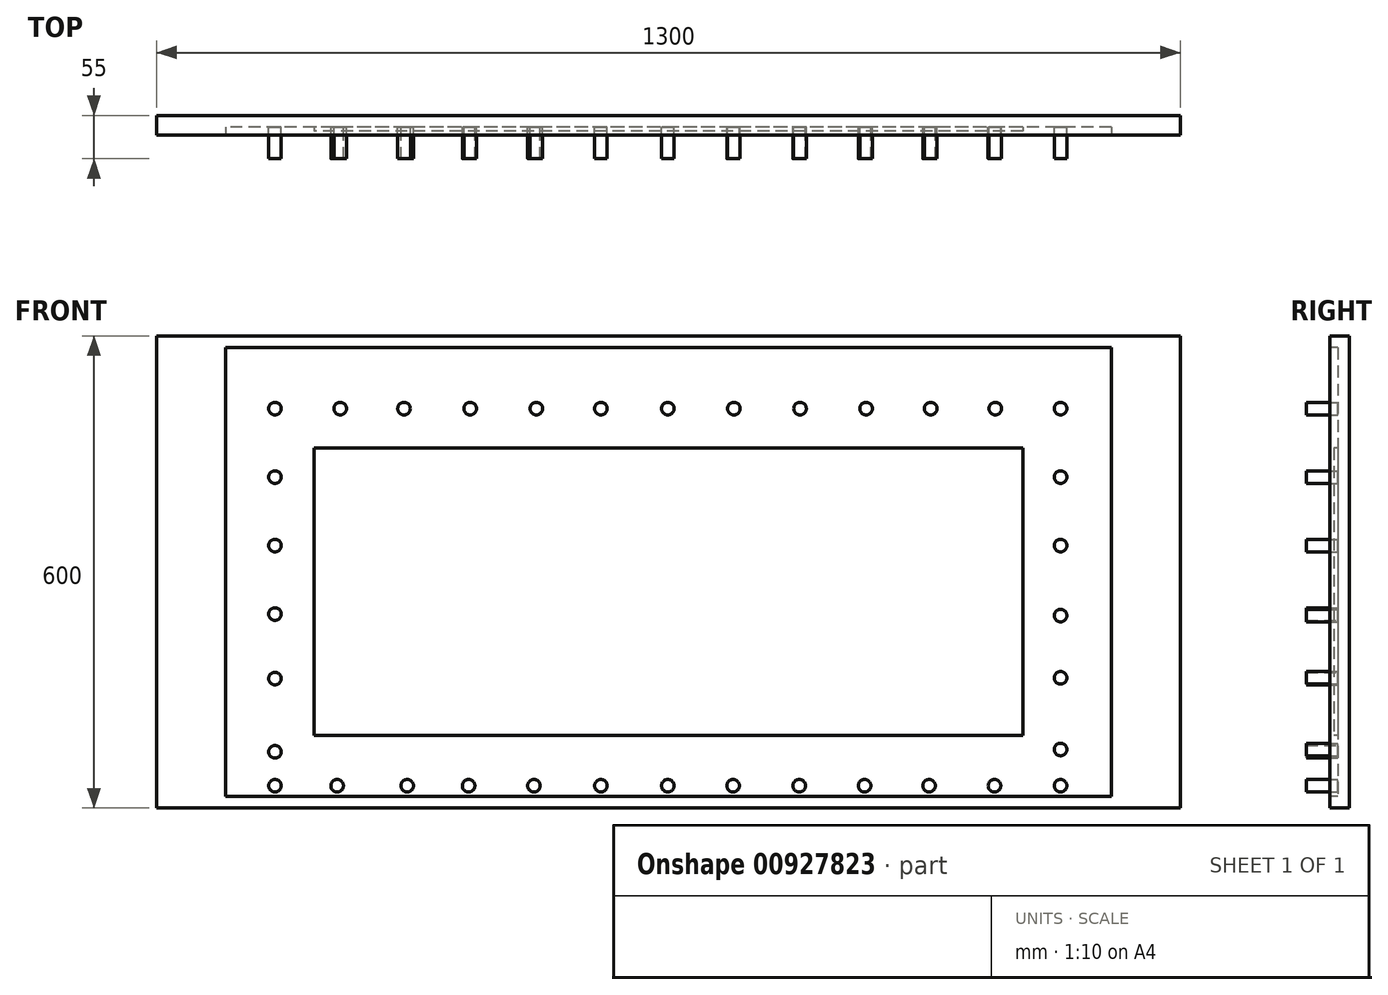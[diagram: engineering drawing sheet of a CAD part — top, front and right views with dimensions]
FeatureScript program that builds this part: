
annotation { "Feature Type Name" : "Feature", "Feature Type Description" : "" }
export const myFeature = defineFeature(function(context is Context, id is Id, definition is map)
    precondition{}
    {
        {
            var Q0;
            Q0=qCreatedBy(makeId("Front.planeOp"),FACE);
            var sketch = newSketch(context, id + "F0", { "sketchPlane" : qUnion([Q0])});
            skLineSegment(sketch, "E0.bottom", {"start": v(-600, 280) * mm, "end": v(600, 280) * mm});
            skLineSegment(sketch, "E0.top", {"start": v(-600, -280) * mm, "end": v(600, -280) * mm});
            skLineSegment(sketch, "E0.left", {"start": v(-600, 280) * mm, "end": v(-600, -280) * mm});
            skLineSegment(sketch, "E0.right", {"start": v(600, 280) * mm, "end": v(600, -280) * mm});
            skPoint(sketch, "E0.middle", {"position": v(0, 0) * mm});
            skCircle(sketch, "E1", {"center": v(550, 237.5) * mm, "radius": 9 * mm});
            skLineSegment(sketch, "E2", {"start": v(550, 237.5) * mm, "end": v(425, 237.5) * mm, "construction": true});
            skLineSegment(sketch, "E3", {"start": v(425, 237.5) * mm, "end": v(340, 237.5) * mm, "construction": true});
            skCircle(sketch, "E4", {"center": v(425, 237.5) * mm, "radius": 9 * mm});
            skCircle(sketch, "E5", {"center": v(340, 237.5) * mm, "radius": 9 * mm});
            skLineSegment(sketch, "E6", {"start": v(340, 237.5) * mm, "end": v(255, 237.5) * mm, "construction": true});
            skLineSegment(sketch, "E7", {"start": v(255, 237.5) * mm, "end": v(170, 237.5) * mm, "construction": true});
            skLineSegment(sketch, "E8", {"start": v(170, 237.5) * mm, "end": v(85, 237.5) * mm, "construction": true});
            skLineSegment(sketch, "E9", {"start": v(85, 237.5) * mm, "end": v(0, 237.5) * mm, "construction": true});
            skLineSegment(sketch, "E10", {"start": v(0, 237.5) * mm, "end": v(-85, 237.5) * mm, "construction": true});
            skLineSegment(sketch, "E11", {"start": v(-85, 237.5) * mm, "end": v(-170, 237.5) * mm, "construction": true});
            skLineSegment(sketch, "E12", {"start": v(-170, 237.5) * mm, "end": v(-255, 237.5) * mm, "construction": true});
            skLineSegment(sketch, "E13", {"start": v(-255, 237.5) * mm, "end": v(-340, 237.5) * mm, "construction": true});
            skLineSegment(sketch, "E14", {"start": v(-340, 237.5) * mm, "end": v(-425, 237.5) * mm, "construction": true});
            skLineSegment(sketch, "E15", {"start": v(-425, 237.5) * mm, "end": v(-550, 237.5) * mm, "construction": true});
            skCircle(sketch, "E16", {"center": v(255, 237.5) * mm, "radius": 9 * mm});
            skCircle(sketch, "E17", {"center": v(170, 237.5) * mm, "radius": 9 * mm});
            skCircle(sketch, "E18", {"center": v(85, 237.5) * mm, "radius": 9 * mm});
            skCircle(sketch, "E19", {"center": v(0, 237.5) * mm, "radius": 9 * mm});
            skCircle(sketch, "E20", {"center": v(-85, 237.5) * mm, "radius": 9 * mm});
            skCircle(sketch, "E21", {"center": v(-170, 237.5) * mm, "radius": 9 * mm});
            skCircle(sketch, "E22", {"center": v(-255, 237.5) * mm, "radius": 9 * mm});
            skCircle(sketch, "E23", {"center": v(-340, 237.5) * mm, "radius": 9 * mm});
            skCircle(sketch, "E24", {"center": v(-425, 237.5) * mm, "radius": 9 * mm});
            skCircle(sketch, "E25", {"center": v(-550, 237.5) * mm, "radius": 9 * mm});
            skLineSegment(sketch, "E26", {"start": v(0, 0) * mm, "end": v(136, 0) * mm, "construction": true});
            skLineSegment(sketch, "E27", {"start": v(0, 0) * mm, "end": v(0, -117.51) * mm, "construction": true});
            skCircle(sketch, "E28.MirrorC", {"center": v(0, -237.5) * mm, "radius": 9 * mm});
            skCircle(sketch, "E29.MirrorC", {"center": v(425, -237.5) * mm, "radius": 9 * mm});
            skCircle(sketch, "E30.MirrorC", {"center": v(340, -237.5) * mm, "radius": 9 * mm});
            skCircle(sketch, "E31.MirrorC", {"center": v(-425, -237.5) * mm, "radius": 9 * mm});
            skCircle(sketch, "E32.MirrorC", {"center": v(85, -237.5) * mm, "radius": 9 * mm});
            skCircle(sketch, "E33.MirrorC", {"center": v(-340, -237.5) * mm, "radius": 9 * mm});
            skCircle(sketch, "E34.MirrorC", {"center": v(-170, -237.5) * mm, "radius": 9 * mm});
            skCircle(sketch, "E35.MirrorC", {"center": v(255, -237.5) * mm, "radius": 9 * mm});
            skCircle(sketch, "E36.MirrorC", {"center": v(-85, -237.5) * mm, "radius": 9 * mm});
            skCircle(sketch, "E37.MirrorC", {"center": v(170, -237.5) * mm, "radius": 9 * mm});
            skCircle(sketch, "E38.MirrorC", {"center": v(-255, -237.5) * mm, "radius": 9 * mm});
            skCircle(sketch, "E39.MirrorC", {"center": v(-550, -237.5) * mm, "radius": 9 * mm});
            skCircle(sketch, "E40.MirrorC", {"center": v(550, -237.5) * mm, "radius": 9 * mm});
            skLineSegment(sketch, "E41.MirrorCS", {"start": v(0, -237.5) * mm, "end": v(-85, -237.5) * mm, "construction": true});
            skLineSegment(sketch, "E42.MirrorCS", {"start": v(340, -237.5) * mm, "end": v(255, -237.5) * mm, "construction": true});
            skLineSegment(sketch, "E43.MirrorCS", {"start": v(170, -237.5) * mm, "end": v(85, -237.5) * mm, "construction": true});
            skLineSegment(sketch, "E44.MirrorCS", {"start": v(-255, -237.5) * mm, "end": v(-340, -237.5) * mm, "construction": true});
            skLineSegment(sketch, "E45.MirrorCS", {"start": v(-85, -237.5) * mm, "end": v(-170, -237.5) * mm, "construction": true});
            skLineSegment(sketch, "E46.MirrorCS", {"start": v(85, -237.5) * mm, "end": v(0, -237.5) * mm, "construction": true});
            skLineSegment(sketch, "E47.MirrorCS", {"start": v(-170, -237.5) * mm, "end": v(-255, -237.5) * mm, "construction": true});
            skLineSegment(sketch, "E48.MirrorCS", {"start": v(425, -237.5) * mm, "end": v(340, -237.5) * mm, "construction": true});
            skLineSegment(sketch, "E49.MirrorCS", {"start": v(550, -237.5) * mm, "end": v(425, -237.5) * mm, "construction": true});
            skLineSegment(sketch, "E50.MirrorCS", {"start": v(-340, -237.5) * mm, "end": v(-425, -237.5) * mm, "construction": true});
            skLineSegment(sketch, "E51.MirrorCS", {"start": v(-425, -237.5) * mm, "end": v(-550, -237.5) * mm, "construction": true});
            skLineSegment(sketch, "E52.MirrorCS", {"start": v(255, -237.5) * mm, "end": v(170, -237.5) * mm, "construction": true});
            skLineSegment(sketch, "E53", {"start": v(550, -237.5) * mm, "end": v(550, -187.5) * mm, "construction": true});
            skLineSegment(sketch, "E54", {"start": v(550, -187.5) * mm, "end": v(550, -102.5) * mm, "construction": true});
            skLineSegment(sketch, "E55", {"start": v(550, -102.5) * mm, "end": v(550, -17.5) * mm, "construction": true});
            skLineSegment(sketch, "E56", {"start": v(550, -17.5) * mm, "end": v(550, 67.5) * mm, "construction": true});
            skLineSegment(sketch, "E57", {"start": v(550, 67.5) * mm, "end": v(550, 152.5) * mm, "construction": true});
            skCircle(sketch, "E58", {"center": v(550, 152.5) * mm, "radius": 9 * mm});
            skCircle(sketch, "E59", {"center": v(550, 67.5) * mm, "radius": 9 * mm});
            skCircle(sketch, "E60", {"center": v(550, -17.5) * mm, "radius": 9 * mm});
            skCircle(sketch, "E61", {"center": v(550, -102.5) * mm, "radius": 9 * mm});
            skCircle(sketch, "E62", {"center": v(550, -187.5) * mm, "radius": 9 * mm});
            skCircle(sketch, "E63.MirrorC", {"center": v(-550, 152.5) * mm, "radius": 9 * mm});
            skLineSegment(sketch, "E64.MirrorCS", {"start": v(-550, -187.5) * mm, "end": v(-550, -102.5) * mm, "construction": true});
            skLineSegment(sketch, "E65.MirrorCS", {"start": v(-550, -17.5) * mm, "end": v(-550, 67.5) * mm, "construction": true});
            skCircle(sketch, "E66.MirrorC", {"center": v(-550, -187.5) * mm, "radius": 9 * mm});
            skCircle(sketch, "E67.MirrorC", {"center": v(-550, -17.5) * mm, "radius": 9 * mm});
            skCircle(sketch, "E68.MirrorC", {"center": v(-550, 67.5) * mm, "radius": 9 * mm});
            skLineSegment(sketch, "E69.MirrorCS", {"start": v(-550, -102.5) * mm, "end": v(-550, -17.5) * mm, "construction": true});
            skLineSegment(sketch, "E70.MirrorCS", {"start": v(-550, 67.5) * mm, "end": v(-550, 152.5) * mm, "construction": true});
            skCircle(sketch, "E71.MirrorC", {"center": v(-550, -102.5) * mm, "radius": 9 * mm});
            skSolve(sketch);
        }
        {
            var Q0;
            Q0 = qSketchRegion(id + "F0", true);
            extrude(context, id + "F1", {"entities" : qUnion([Q0]), "depth" : 20 * mm, "offsetDistance" : 25 * mm});
        }
        {
            var Q0;
            Q0=qCreatedBy(makeId("Front.planeOp"),FACE);
            var sketch = newSketch(context, id + "F2", { "sketchPlane" : qUnion([Q0])});
            skLineSegment(sketch, "E72.bottom", {"start": v(650, 300) * mm, "end": v(-650, 300) * mm});
            skLineSegment(sketch, "E72.top", {"start": v(650, -300) * mm, "end": v(-650, -300) * mm});
            skLineSegment(sketch, "E72.left", {"start": v(650, 300) * mm, "end": v(650, -300) * mm});
            skLineSegment(sketch, "E72.right", {"start": v(-650, 300) * mm, "end": v(-650, -300) * mm});
            skPoint(sketch, "E72.middle", {"position": v(0, 0) * mm});
            skLineSegment(sketch, "E73.bottom", {"start": v(450, 157.5) * mm, "end": v(-450, 157.5) * mm});
            skLineSegment(sketch, "E74", {"start": v(450, 157.5) * mm, "end": v(450, -207.5) * mm});
            skLineSegment(sketch, "E75", {"start": v(450, -207.5) * mm, "end": v(-450, -207.5) * mm});
            skLineSegment(sketch, "E76", {"start": v(-450, -207.5) * mm, "end": v(-450, 157.5) * mm});
            skSolve(sketch);
        }
        {
            var Q0;
            Q0 = qSketchRegion(id + "F2", true);
            extrude(context, id + "F3", {"entities" : qUnion([Q0]), "depth" : 25 * mm, "offsetDistance" : 25 * mm});
        }
        {
            var Q0;
            Q0=makeQuery(id+"F3.opExtrude","CAP_FACE",FACE,{"disambiguationData":[OSD([sQuery(id+"F2.wireOp",EDGE,"E72.bottom"),sQuery(id+"F2.wireOp",EDGE,"E72.top"),sQuery(id+"F2.wireOp",EDGE,"E72.left"),sQuery(id+"F2.wireOp",EDGE,"E72.right"),sQuery(id+"F2.wireOp",EDGE,"E73.bottom"),sQuery(id+"F2.wireOp",EDGE,"E73.top"),sQuery(id+"F2.wireOp",EDGE,"E73.left"),sQuery(id+"F2.wireOp",EDGE,"E73.right")])],"isStart":false});
            var sketch = newSketch(context, id + "F4", { "sketchPlane" : qUnion([Q0])});
            skLineSegment(sketch, "E77.bottom", {"start": v(450, 157.5) * mm, "end": v(-450, 157.5) * mm});
            skPoint(sketch, "E77.middle", {"position": v(0, 0) * mm});
            skLineSegment(sketch, "E78.bottom", {"start": v(562.5, 285) * mm, "end": v(-562.5, 285) * mm});
            skLineSegment(sketch, "E78.top", {"start": v(562.5, -285) * mm, "end": v(-562.5, -285) * mm});
            skLineSegment(sketch, "E78.left", {"start": v(562.5, 285) * mm, "end": v(562.5, -285) * mm});
            skLineSegment(sketch, "E78.right", {"start": v(-562.5, 285) * mm, "end": v(-562.5, -285) * mm});
            skLineSegment(sketch, "E79", {"start": v(-450, 157.5) * mm, "end": v(-450, -207.5) * mm});
            skLineSegment(sketch, "E80", {"start": v(-450, -207.5) * mm, "end": v(450, -207.5) * mm});
            skLineSegment(sketch, "E81", {"start": v(450, -207.5) * mm, "end": v(450, 157.5) * mm});
            skSolve(sketch);
        }
        {
            var Q0;
            Q0 = qSketchRegion(id + "F4", true);
            extrude(context, id + "F5", {"entities" : qUnion([Q0]), "operationType" : NewBodyOperationType.REMOVE, "oppositeDirection" : true, "depth" : 10 * mm, "offsetDistance" : 25 * mm});
        }
        {
            var Q0;
            Q0=makeQuery(id+"F5.boolean.opBoolean","COPY",FACE,{"derivedFrom":makeQuery(id+"F5.opExtrude","CAP_FACE",FACE,{"disambiguationData":[OSD([sQuery(id+"F4.wireOp",EDGE,"E77.bottom"),sQuery(id+"F4.wireOp",EDGE,"E78.bottom"),sQuery(id+"F4.wireOp",EDGE,"E78.top"),sQuery(id+"F4.wireOp",EDGE,"E78.left"),sQuery(id+"F4.wireOp",EDGE,"E78.right"),sQuery(id+"F4.wireOp",EDGE,"E79"),sQuery(id+"F4.wireOp",EDGE,"E80"),sQuery(id+"F4.wireOp",EDGE,"E81")])],"isStart":false})});
            var sketch = newSketch(context, id + "F6", { "sketchPlane" : qUnion([Q0])});
            skCircle(sketch, "E82", {"center": v(-500, 207.5) * mm, "radius": 8 * mm});
            skLineSegment(sketch, "E83", {"start": v(-500, 207.5) * mm, "end": v(-500, 120.5) * mm, "construction": true});
            skLineSegment(sketch, "E84", {"start": v(-500, 120.5) * mm, "end": v(-500, 33.5) * mm, "construction": true});
            skLineSegment(sketch, "E85", {"start": v(-500, 33.5) * mm, "end": v(-500, -53.5) * mm, "construction": true});
            skLineSegment(sketch, "E86", {"start": v(-500, -53.5) * mm, "end": v(-500, -135.5) * mm, "construction": true});
            skLineSegment(sketch, "E87", {"start": v(-500, -135.5) * mm, "end": v(-500, -228.5) * mm, "construction": true});
            skLineSegment(sketch, "E88", {"start": v(-500, -228.5) * mm, "end": v(-500, -271.5) * mm, "construction": true});
            skLineSegment(sketch, "E89", {"start": v(-500, 207.5) * mm, "end": v(-417, 207.5) * mm, "construction": true});
            skLineSegment(sketch, "E90", {"start": v(-417, 207.5) * mm, "end": v(-336, 207.5) * mm, "construction": true});
            skLineSegment(sketch, "E91", {"start": v(-336, 207.5) * mm, "end": v(-252, 207.5) * mm, "construction": true});
            skLineSegment(sketch, "E92", {"start": v(-252, 207.5) * mm, "end": v(-168, 207.5) * mm, "construction": true});
            skLineSegment(sketch, "E93", {"start": v(-168, 207.5) * mm, "end": v(-86, 207.5) * mm, "construction": true});
            skLineSegment(sketch, "E94", {"start": v(-86, 207.5) * mm, "end": v(-1, 207.5) * mm, "construction": true});
            skLineSegment(sketch, "E95", {"start": v(-1, 207.5) * mm, "end": v(83, 207.5) * mm, "construction": true});
            skLineSegment(sketch, "E96", {"start": v(83, 207.5) * mm, "end": v(167, 207.5) * mm, "construction": true});
            skLineSegment(sketch, "E97", {"start": v(167, 207.5) * mm, "end": v(251, 207.5) * mm, "construction": true});
            skLineSegment(sketch, "E98", {"start": v(251, 207.5) * mm, "end": v(333, 207.5) * mm, "construction": true});
            skLineSegment(sketch, "E99", {"start": v(333, 207.5) * mm, "end": v(415, 207.5) * mm, "construction": true});
            skLineSegment(sketch, "E100", {"start": v(415, 207.5) * mm, "end": v(498, 207.5) * mm, "construction": true});
            skLineSegment(sketch, "E101", {"start": v(498, 207.5) * mm, "end": v(498, 120.5) * mm, "construction": true});
            skLineSegment(sketch, "E102", {"start": v(498, 120.5) * mm, "end": v(498, 33.5) * mm, "construction": true});
            skLineSegment(sketch, "E103", {"start": v(498, 33.5) * mm, "end": v(498, -55.5) * mm, "construction": true});
            skLineSegment(sketch, "E104", {"start": v(498, -55.5) * mm, "end": v(498, -134.5) * mm, "construction": true});
            skLineSegment(sketch, "E105", {"start": v(498, -134.5) * mm, "end": v(498, -225.5) * mm, "construction": true});
            skLineSegment(sketch, "E106", {"start": v(498, -225.5) * mm, "end": v(498, -271.5) * mm, "construction": true});
            skLineSegment(sketch, "E107", {"start": v(-500, -271.5) * mm, "end": v(-421, -271.5) * mm, "construction": true});
            skLineSegment(sketch, "E108", {"start": v(-421, -271.5) * mm, "end": v(-332, -271.5) * mm, "construction": true});
            skLineSegment(sketch, "E109", {"start": v(-332, -271.5) * mm, "end": v(-254, -271.5) * mm, "construction": true});
            skLineSegment(sketch, "E110", {"start": v(-254, -271.5) * mm, "end": v(-171, -271.5) * mm, "construction": true});
            skLineSegment(sketch, "E111", {"start": v(-171, -271.5) * mm, "end": v(-86, -271.5) * mm, "construction": true});
            skLineSegment(sketch, "E112", {"start": v(-86, -271.5) * mm, "end": v(-1, -271.5) * mm, "construction": true});
            skLineSegment(sketch, "E113", {"start": v(-1, -271.5) * mm, "end": v(82, -271.5) * mm, "construction": true});
            skLineSegment(sketch, "E114", {"start": v(82, -271.5) * mm, "end": v(166, -271.5) * mm, "construction": true});
            skLineSegment(sketch, "E115", {"start": v(166, -271.5) * mm, "end": v(249, -271.5) * mm, "construction": true});
            skLineSegment(sketch, "E116", {"start": v(249, -271.5) * mm, "end": v(331, -271.5) * mm, "construction": true});
            skLineSegment(sketch, "E117", {"start": v(331, -271.5) * mm, "end": v(414, -271.5) * mm, "construction": true});
            skLineSegment(sketch, "E118", {"start": v(414, -271.5) * mm, "end": v(498, -271.5) * mm, "construction": true});
            skCircle(sketch, "E119", {"center": v(-500, 120.5) * mm, "radius": 8 * mm});
            skCircle(sketch, "E120", {"center": v(-500, 33.5) * mm, "radius": 8 * mm});
            skCircle(sketch, "E121", {"center": v(-500, -53.5) * mm, "radius": 8 * mm});
            skCircle(sketch, "E122", {"center": v(-500, -135.5) * mm, "radius": 8 * mm});
            skCircle(sketch, "E123", {"center": v(-500, -228.5) * mm, "radius": 8 * mm});
            skCircle(sketch, "E124", {"center": v(-500, -271.5) * mm, "radius": 8 * mm});
            skCircle(sketch, "E125", {"center": v(-421, -271.5) * mm, "radius": 8 * mm});
            skCircle(sketch, "E126", {"center": v(-332, -271.5) * mm, "radius": 8 * mm});
            skCircle(sketch, "E127", {"center": v(-254, -271.5) * mm, "radius": 8 * mm});
            skCircle(sketch, "E128", {"center": v(-171, -271.5) * mm, "radius": 8 * mm});
            skCircle(sketch, "E129", {"center": v(-86, -271.5) * mm, "radius": 8 * mm});
            skCircle(sketch, "E130", {"center": v(-1, -271.5) * mm, "radius": 8 * mm});
            skCircle(sketch, "E131", {"center": v(82, -271.5) * mm, "radius": 8 * mm});
            skCircle(sketch, "E132", {"center": v(166, -271.5) * mm, "radius": 8 * mm});
            skCircle(sketch, "E133", {"center": v(249, -271.5) * mm, "radius": 8 * mm});
            skCircle(sketch, "E134", {"center": v(414, -271.5) * mm, "radius": 8 * mm});
            skCircle(sketch, "E135", {"center": v(498, -271.5) * mm, "radius": 8 * mm});
            skCircle(sketch, "E136", {"center": v(331, -271.5) * mm, "radius": 8 * mm});
            skCircle(sketch, "E137", {"center": v(498, -225.5) * mm, "radius": 8 * mm});
            skCircle(sketch, "E138", {"center": v(498, -134.5) * mm, "radius": 8 * mm});
            skCircle(sketch, "E139", {"center": v(498, -55.5) * mm, "radius": 8 * mm});
            skCircle(sketch, "E140", {"center": v(498, 33.5) * mm, "radius": 8 * mm});
            skCircle(sketch, "E141", {"center": v(498, 120.5) * mm, "radius": 8 * mm});
            skCircle(sketch, "E142", {"center": v(498, 207.5) * mm, "radius": 8 * mm});
            skCircle(sketch, "E143", {"center": v(415, 207.5) * mm, "radius": 8 * mm});
            skCircle(sketch, "E144", {"center": v(333, 207.5) * mm, "radius": 8 * mm});
            skCircle(sketch, "E145", {"center": v(251, 207.5) * mm, "radius": 8 * mm});
            skCircle(sketch, "E146", {"center": v(167, 207.5) * mm, "radius": 8 * mm});
            skCircle(sketch, "E147", {"center": v(83, 207.5) * mm, "radius": 8 * mm});
            skCircle(sketch, "E148", {"center": v(-1, 207.5) * mm, "radius": 8 * mm});
            skCircle(sketch, "E149", {"center": v(-86, 207.5) * mm, "radius": 8 * mm});
            skCircle(sketch, "E150", {"center": v(-168, 207.5) * mm, "radius": 8 * mm});
            skCircle(sketch, "E151", {"center": v(-252, 207.5) * mm, "radius": 8 * mm});
            skCircle(sketch, "E152", {"center": v(-336, 207.5) * mm, "radius": 8 * mm});
            skCircle(sketch, "E153", {"center": v(-417, 207.5) * mm, "radius": 8 * mm});
            skSolve(sketch);
        }
        {
            var Q0;
            Q0 = qSketchRegion(id + "F6", true);
            extrude(context, id + "F7", {"entities" : qUnion([Q0]), "operationType" : NewBodyOperationType.ADD, "depth" : 40 * mm, "offsetDistance" : 25 * mm});
        }
    });
